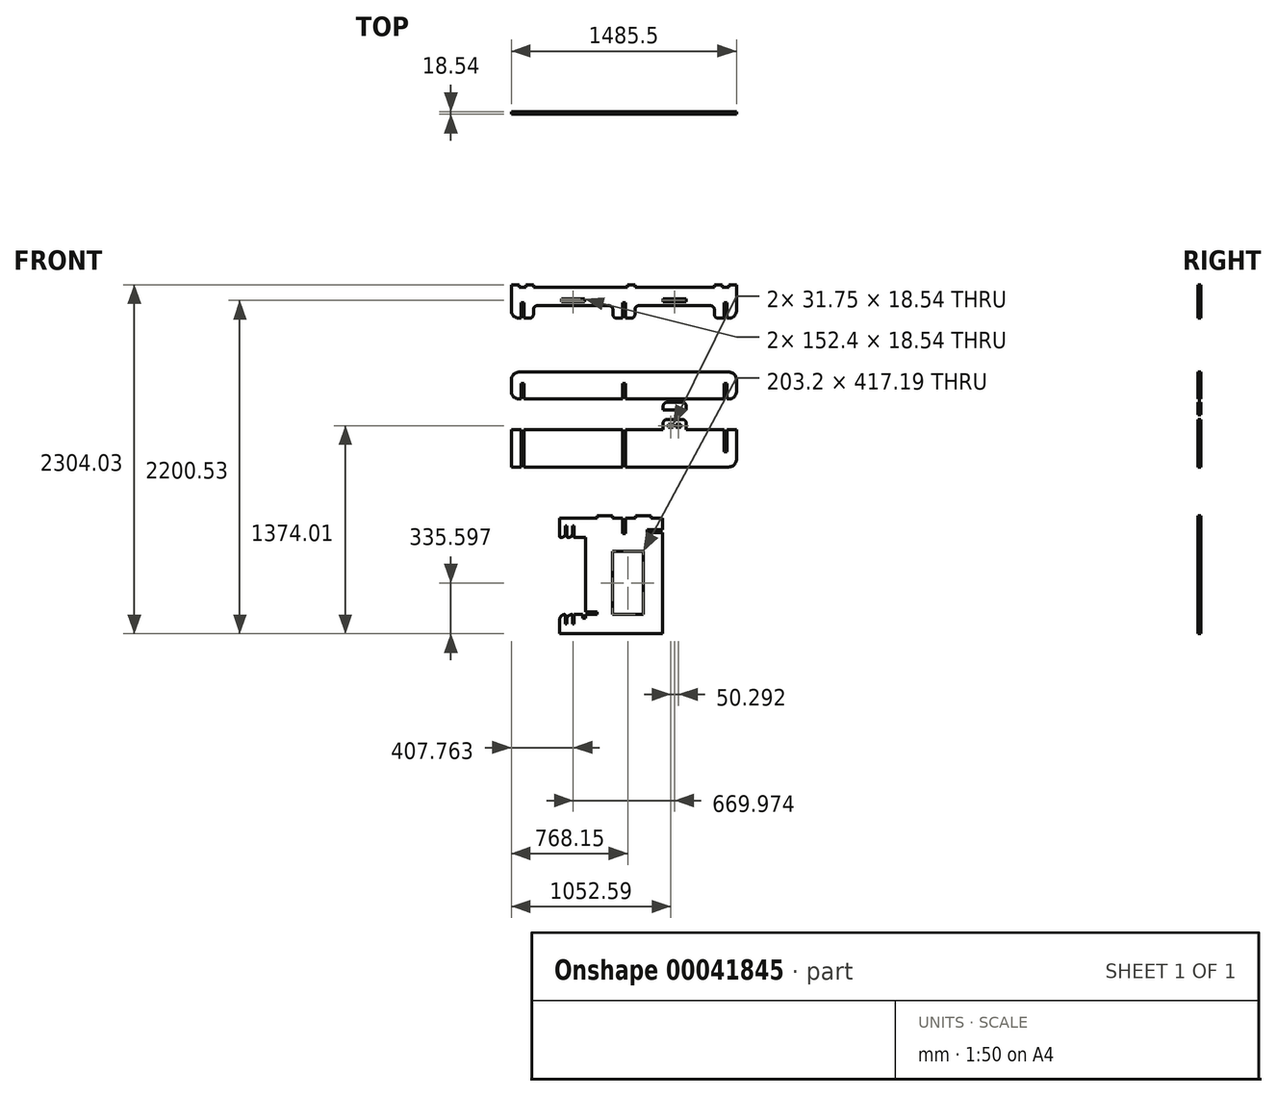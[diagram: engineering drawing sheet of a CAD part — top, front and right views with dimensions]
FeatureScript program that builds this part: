
annotation { "Feature Type Name" : "Feature", "Feature Type Description" : "" }
export const myFeature = defineFeature(function(context is Context, id is Id, definition is map)
    precondition{}
    {
        {
            var Q0;
            Q0=qCreatedBy(makeId("Front.planeOp"),FACE);
            var sketch = newSketch(context, id + "F0", { "sketchPlane" : qUnion([Q0])});
            skLineSegment(sketch, "E0.bottom", {"start": v(-254, 381) * mm, "end": v(-177.8, 381) * mm});
            skLineSegment(sketch, "E0.top", {"start": v(-254, -381) * mm, "end": v(254, -381) * mm});
            skLineSegment(sketch, "E0.left", {"start": v(-254, 254) * mm, "end": v(-254, -235.46) * mm});
            skLineSegment(sketch, "E0.right", {"start": v(254, 381) * mm, "end": v(254, -381) * mm});
            skLineSegment(sketch, "E1.bottom", {"start": v(-254, 381) * mm, "end": v(-423.33, 381) * mm});
            skLineSegment(sketch, "E1.top", {"start": v(-254, 254) * mm, "end": v(-323, 254) * mm});
            skLineSegment(sketch, "E1.right", {"start": v(-423.33, 381) * mm, "end": v(-423.33, 260.35) * mm});
            skLineSegment(sketch, "E2", {"start": v(-254, 0) * mm, "end": v(254, 0) * mm, "construction": true});
            skLineSegment(sketch, "E3", {"start": v(-423.33, 317.5) * mm, "end": v(-385.23, 317.5) * mm, "construction": true});
            skLineSegment(sketch, "E4.top", {"start": v(-385.23, 317.5) * mm, "end": v(-376.34, 317.5) * mm});
            skLineSegment(sketch, "E4.left", {"start": v(-385.23, 254) * mm, "end": v(-385.23, 317.5) * mm});
            skLineSegment(sketch, "E4.right", {"start": v(-376.34, 260.35) * mm, "end": v(-376.34, 317.5) * mm});
            skLineSegment(sketch, "E5", {"start": v(-376.34, 317.5) * mm, "end": v(-338.24, 317.5) * mm, "construction": true});
            skLineSegment(sketch, "E6.top", {"start": v(-338.24, 317.5) * mm, "end": v(-329.35, 317.5) * mm});
            skLineSegment(sketch, "E6.left", {"start": v(-338.24, 254) * mm, "end": v(-338.24, 317.5) * mm});
            skLineSegment(sketch, "E6.right", {"start": v(-329.35, 260.35) * mm, "end": v(-329.35, 317.5) * mm});
            skLineSegment(sketch, "E7.trimOffspring", {"start": v(-385.23, 254) * mm, "end": v(-416.98, 254) * mm});
            skLineSegment(sketch, "E8.trimOffspring", {"start": v(-338.24, 254) * mm, "end": v(-370, 254) * mm});
            skLineSegment(sketch, "E9.MirrorCS", {"start": v(-391.58, -254) * mm, "end": v(-423.33, -254) * mm});
            skLineSegment(sketch, "E10.MirrorCS", {"start": v(-376.34, -317.5) * mm, "end": v(-338.24, -317.5) * mm, "construction": true});
            skLineSegment(sketch, "E11.MirrorCS", {"start": v(-423.33, -317.5) * mm, "end": v(-385.23, -317.5) * mm, "construction": true});
            skLineSegment(sketch, "E12.MirrorCS", {"start": v(-338.24, -260.35) * mm, "end": v(-338.24, -317.5) * mm});
            skLineSegment(sketch, "E13.MirrorCS", {"start": v(-344.6, -254) * mm, "end": v(-376.34, -254) * mm});
            skLineSegment(sketch, "E14.MirrorCS", {"start": v(-423.33, -381) * mm, "end": v(-423.33, -254) * mm});
            skLineSegment(sketch, "E15.MirrorCS", {"start": v(-376.34, -254) * mm, "end": v(-376.34, -317.5) * mm});
            skLineSegment(sketch, "E16.MirrorCS", {"start": v(-385.23, -260.35) * mm, "end": v(-385.23, -317.5) * mm});
            skLineSegment(sketch, "E17.MirrorCS", {"start": v(-254, -381) * mm, "end": v(-423.33, -381) * mm});
            skLineSegment(sketch, "E18.MirrorCS", {"start": v(-385.23, -317.5) * mm, "end": v(-376.34, -317.5) * mm});
            skLineSegment(sketch, "E19.MirrorCS", {"start": v(-338.24, -317.5) * mm, "end": v(-329.35, -317.5) * mm});
            skLineSegment(sketch, "E20.MirrorCS", {"start": v(-329.35, -254) * mm, "end": v(-329.35, -317.5) * mm});
            skLineSegment(sketch, "E21.top", {"start": v(-177.8, 399.14) * mm, "end": v(-76.2, 399.14) * mm});
            skLineSegment(sketch, "E21.left", {"start": v(-177.8, 381) * mm, "end": v(-177.8, 399.14) * mm});
            skLineSegment(sketch, "E21.right", {"start": v(-76.2, 381) * mm, "end": v(-76.2, 399.14) * mm});
            skLineSegment(sketch, "E22", {"start": v(0, 381) * mm, "end": v(0, -381) * mm, "construction": true});
            skLineSegment(sketch, "E23.MirrorCS", {"start": v(177.8, 381) * mm, "end": v(177.8, 399.14) * mm});
            skLineSegment(sketch, "E24.MirrorCS", {"start": v(76.2, 381) * mm, "end": v(76.2, 399.14) * mm});
            skLineSegment(sketch, "E25.MirrorCS", {"start": v(177.8, 399.14) * mm, "end": v(76.2, 399.14) * mm});
            skLineSegment(sketch, "E26.left", {"start": v(-9.07, 381) * mm, "end": v(-9.07, 279.4) * mm});
            skPoint(sketch, "E27", {"position": v(0, 279.4) * mm});
            skLineSegment(sketch, "E26.right", {"start": v(9.07, 381) * mm, "end": v(9.07, 279.4) * mm});
            skPoint(sketch, "E28", {"position": v(0, 381) * mm});
            skLineSegment(sketch, "E26.bottom", {"start": v(-9.07, 381) * mm, "end": v(9.07, 381) * mm});
            skLineSegment(sketch, "E26.top", {"start": v(-9.07, 279.4) * mm, "end": v(9.07, 279.4) * mm});
            skLineSegment(sketch, "E29", {"start": v(25.4, 381) * mm, "end": v(25.4, 163.2) * mm, "construction": true});
            skLineSegment(sketch, "E30", {"start": v(254, -45.4) * mm, "end": v(127, -45.4) * mm, "construction": true});
            skLineSegment(sketch, "E31", {"start": v(0, -381) * mm, "end": v(0, -254) * mm, "construction": true});
            skLineSegment(sketch, "E32.bottom", {"start": v(-76.2, 163.2) * mm, "end": v(127, 163.2) * mm});
            skLineSegment(sketch, "E32.top", {"start": v(-76.2, -254) * mm, "end": v(127, -254) * mm});
            skLineSegment(sketch, "E32.left", {"start": v(-76.2, 163.2) * mm, "end": v(-76.2, -254) * mm});
            skLineSegment(sketch, "E32.right", {"start": v(127, 163.2) * mm, "end": v(127, -254) * mm});
            skLineSegment(sketch, "E33.right", {"start": v(-177.8, -254) * mm, "end": v(-177.8, -235.46) * mm});
            skLineSegment(sketch, "E34", {"start": v(-177.8, -235.46) * mm, "end": v(-254, -235.46) * mm});
            skPoint(sketch, "E35", {"position": v(0, 0) * mm});
            skLineSegment(sketch, "E36", {"start": v(-329.35, -254) * mm, "end": v(-177.8, -254) * mm});
            skLineSegment(sketch, "E37.trimOffspring", {"start": v(-76.2, 381) * mm, "end": v(76.2, 381) * mm});
            skLineSegment(sketch, "E38.trimOffspring", {"start": v(177.8, 381) * mm, "end": v(254, 381) * mm});
            skLineSegment(sketch, "E39.bottom", {"start": v(-177.8, -235.46) * mm, "end": v(-423.33, -235.46) * mm});
            skLineSegment(sketch, "E39.top", {"start": v(-177.8, -254) * mm, "end": v(-423.33, -254) * mm});
            skLineSegment(sketch, "E39.left", {"start": v(-177.8, -235.46) * mm, "end": v(-177.8, -254) * mm});
            skLineSegment(sketch, "E39.right", {"start": v(-423.33, -235.46) * mm, "end": v(-423.33, -254) * mm});
            skArc(sketch, "E40", {"start": v(-889.07, 2915.45) * mm, "mid": v(-449.45, 3014.68) * mm, "end": v(0, 3048) * mm});
            skArc(sketch, "E41.0", {"start": v(-656.32, 2189.76) * mm, "mid": v(-331.67, 2261.81) * mm, "end": v(0, 2286) * mm, "construction": true});
            skLineSegment(sketch, "E42", {"start": v(0, 3048) * mm, "end": v(0, 2718.2) * mm, "construction": true});
            skLineSegment(sketch, "E43", {"start": v(-719.24, 2222.78) * mm, "end": v(-739.7, 2286) * mm, "construction": true});
            skLineSegment(sketch, "E44", {"start": v(-703.77, 2174.97) * mm, "end": v(0, 0) * mm, "construction": true});
            skArc(sketch, "E45.MirrorCS", {"start": v(889.07, 2915.45) * mm, "mid": v(449.45, 3014.68) * mm, "end": v(0, 3048) * mm});
            skLineSegment(sketch, "E46.MirrorCS", {"start": v(719.24, 2222.78) * mm, "end": v(739.7, 2286) * mm, "construction": true});
            skArc(sketch, "E47.MirrorCS", {"start": v(656.32, 2189.76) * mm, "mid": v(331.67, 2261.81) * mm, "end": v(0, 2286) * mm, "construction": true});
            skLineSegment(sketch, "E48.MirrorCS", {"start": v(-9.27, 2362.2) * mm, "end": v(9.27, 2362.2) * mm});
            skLineSegment(sketch, "E49.MirrorCS", {"start": v(-9.27, 2362.2) * mm, "end": v(-9.27, 2463.8) * mm});
            skLineSegment(sketch, "E50.MirrorCS", {"start": v(-9.27, 2463.8) * mm, "end": v(9.27, 2463.8) * mm});
            skLineSegment(sketch, "E51.MirrorCS", {"start": v(9.27, 2362.2) * mm, "end": v(9.27, 2463.8) * mm});
            skLineSegment(sketch, "E52.left", {"start": v(-72.77, 2530.93) * mm, "end": v(-72.77, 2549.47) * mm});
            skLineSegment(sketch, "E52.bottom", {"start": v(-72.77, 2530.93) * mm, "end": v(-21.97, 2530.93) * mm});
            skLineSegment(sketch, "E52.top", {"start": v(-72.77, 2549.47) * mm, "end": v(-21.97, 2549.47) * mm});
            skLineSegment(sketch, "E52.right", {"start": v(-21.97, 2530.93) * mm, "end": v(-21.97, 2549.47) * mm});
            skPoint(sketch, "E53", {"position": v(-21.97, 2540.2) * mm});
            skLineSegment(sketch, "E54", {"start": v(0, 2286) * mm, "end": v(0, 2362.2) * mm});
            skPoint(sketch, "E55", {"position": v(0, 2362.2) * mm});
            skLineSegment(sketch, "E56", {"start": v(-9.27, 2463.8) * mm, "end": v(-9.27, 2530.93) * mm, "construction": true});
            skLineSegment(sketch, "E57", {"start": v(-9.27, 2530.93) * mm, "end": v(9.27, 2530.93) * mm, "construction": true});
            skPoint(sketch, "E58", {"position": v(0, 2530.93) * mm});
            skLineSegment(sketch, "E59.MirrorCS", {"start": v(21.97, 2530.93) * mm, "end": v(21.97, 2549.47) * mm});
            skPoint(sketch, "E60.MirrorP", {"position": v(21.97, 2540.2) * mm});
            skLineSegment(sketch, "E61.MirrorCS", {"start": v(72.77, 2530.93) * mm, "end": v(21.97, 2530.93) * mm});
            skLineSegment(sketch, "E62.MirrorCS", {"start": v(72.77, 2549.47) * mm, "end": v(21.97, 2549.47) * mm});
            skLineSegment(sketch, "E63.MirrorCS", {"start": v(72.77, 2530.93) * mm, "end": v(72.77, 2549.47) * mm});
            skLineSegment(sketch, "E64", {"start": v(-21.97, 2540.2) * mm, "end": v(21.97, 2540.2) * mm, "construction": true});
            skLineSegment(sketch, "E65.MirrorCS", {"start": v(-9.27, 2616.6) * mm, "end": v(9.27, 2616.6) * mm});
            skLineSegment(sketch, "E66.MirrorCS", {"start": v(9.27, 2718.2) * mm, "end": v(9.27, 2616.6) * mm});
            skLineSegment(sketch, "E67.MirrorCS", {"start": v(-9.27, 2718.2) * mm, "end": v(-9.27, 2616.6) * mm});
            skLineSegment(sketch, "E68.MirrorCS", {"start": v(-9.27, 2718.2) * mm, "end": v(9.27, 2718.2) * mm});
            skLineSegment(sketch, "E69", {"start": v(-764.35, 2362.2) * mm, "end": v(764.35, 2362.2) * mm, "construction": true});
            skLineSegment(sketch, "E70", {"start": v(-818.95, 2530.93) * mm, "end": v(-742.75, 2530.93) * mm, "construction": true});
            skLineSegment(sketch, "E71.trimOffspring", {"start": v(0, 2616.6) * mm, "end": v(0, 2463.8) * mm, "construction": true});
            skLineSegment(sketch, "E72.trimOffspring", {"start": v(0, 2362.2) * mm, "end": v(0, 2286) * mm, "construction": true});
            skLineSegment(sketch, "E73.MirrorCS", {"start": v(-679.25, 2362.2) * mm, "end": v(-660.7, 2362.2) * mm});
            skLineSegment(sketch, "E74.MirrorCS", {"start": v(-679.25, 2362.2) * mm, "end": v(-679.25, 2463.8) * mm});
            skLineSegment(sketch, "E75.MirrorCS", {"start": v(-679.25, 2463.8) * mm, "end": v(-660.7, 2463.8) * mm});
            skLineSegment(sketch, "E76.MirrorCS", {"start": v(-660.7, 2362.2) * mm, "end": v(-660.7, 2463.8) * mm});
            skLineSegment(sketch, "E77.left", {"start": v(-742.75, 2530.93) * mm, "end": v(-742.75, 2549.47) * mm});
            skLineSegment(sketch, "E77.bottom", {"start": v(-742.75, 2530.93) * mm, "end": v(-691.95, 2530.93) * mm});
            skLineSegment(sketch, "E77.top", {"start": v(-742.75, 2549.47) * mm, "end": v(-691.95, 2549.47) * mm});
            skLineSegment(sketch, "E77.right", {"start": v(-691.95, 2530.93) * mm, "end": v(-691.95, 2549.47) * mm});
            skPoint(sketch, "E78", {"position": v(-691.95, 2540.2) * mm});
            skPoint(sketch, "E79", {"position": v(-669.97, 2362.2) * mm});
            skLineSegment(sketch, "E80", {"start": v(-679.25, 2463.8) * mm, "end": v(-679.25, 2530.93) * mm, "construction": true});
            skLineSegment(sketch, "E81", {"start": v(-679.25, 2530.93) * mm, "end": v(-660.7, 2530.93) * mm, "construction": true});
            skPoint(sketch, "E82", {"position": v(-669.97, 2530.93) * mm});
            skLineSegment(sketch, "E83.MirrorCS", {"start": v(-648, 2530.93) * mm, "end": v(-648, 2549.47) * mm});
            skPoint(sketch, "E84.MirrorP", {"position": v(-648, 2540.2) * mm});
            skLineSegment(sketch, "E85.MirrorCS", {"start": v(-597.2, 2530.93) * mm, "end": v(-648, 2530.93) * mm});
            skLineSegment(sketch, "E86.MirrorCS", {"start": v(-597.2, 2549.47) * mm, "end": v(-648, 2549.47) * mm});
            skLineSegment(sketch, "E87.MirrorCS", {"start": v(-597.2, 2530.93) * mm, "end": v(-597.2, 2549.47) * mm});
            skLineSegment(sketch, "E88", {"start": v(-648, 2540.2) * mm, "end": v(-691.95, 2540.2) * mm, "construction": true});
            skLineSegment(sketch, "E89.MirrorCS", {"start": v(-679.25, 2616.6) * mm, "end": v(-660.7, 2616.6) * mm});
            skLineSegment(sketch, "E90.MirrorCS", {"start": v(-660.7, 2718.2) * mm, "end": v(-660.7, 2616.6) * mm});
            skLineSegment(sketch, "E91.MirrorCS", {"start": v(-679.25, 2718.2) * mm, "end": v(-679.25, 2616.6) * mm});
            skLineSegment(sketch, "E92.MirrorCS", {"start": v(-679.25, 2718.2) * mm, "end": v(-660.7, 2718.2) * mm});
            skLineSegment(sketch, "E93.trimOffspring", {"start": v(-669.97, 2463.8) * mm, "end": v(-669.97, 2616.6) * mm, "construction": true});
            skLineSegment(sketch, "E94.MirrorCS", {"start": v(679.25, 2718.2) * mm, "end": v(660.7, 2718.2) * mm});
            skLineSegment(sketch, "E95.MirrorCS", {"start": v(679.25, 2718.2) * mm, "end": v(679.25, 2616.6) * mm});
            skLineSegment(sketch, "E96.MirrorCS", {"start": v(660.7, 2718.2) * mm, "end": v(660.7, 2616.6) * mm});
            skLineSegment(sketch, "E97.MirrorCS", {"start": v(679.25, 2616.6) * mm, "end": v(660.7, 2616.6) * mm});
            skLineSegment(sketch, "E98.MirrorCS", {"start": v(742.75, 2549.47) * mm, "end": v(691.95, 2549.47) * mm});
            skLineSegment(sketch, "E99.MirrorCS", {"start": v(742.75, 2530.93) * mm, "end": v(742.75, 2549.47) * mm});
            skLineSegment(sketch, "E100.MirrorCS", {"start": v(691.95, 2530.93) * mm, "end": v(691.95, 2549.47) * mm});
            skLineSegment(sketch, "E101.MirrorCS", {"start": v(742.75, 2530.93) * mm, "end": v(691.95, 2530.93) * mm});
            skLineSegment(sketch, "E102.MirrorCS", {"start": v(648, 2530.93) * mm, "end": v(648, 2549.47) * mm});
            skLineSegment(sketch, "E103.MirrorCS", {"start": v(597.2, 2549.47) * mm, "end": v(648, 2549.47) * mm});
            skLineSegment(sketch, "E104.MirrorCS", {"start": v(597.2, 2530.93) * mm, "end": v(597.2, 2549.47) * mm});
            skLineSegment(sketch, "E105.MirrorCS", {"start": v(597.2, 2530.93) * mm, "end": v(648, 2530.93) * mm});
            skLineSegment(sketch, "E106.MirrorCS", {"start": v(679.25, 2362.2) * mm, "end": v(660.7, 2362.2) * mm});
            skLineSegment(sketch, "E107.MirrorCS", {"start": v(679.25, 2362.2) * mm, "end": v(679.25, 2463.8) * mm});
            skLineSegment(sketch, "E108.MirrorCS", {"start": v(660.7, 2362.2) * mm, "end": v(660.7, 2463.8) * mm});
            skLineSegment(sketch, "E109.MirrorCS", {"start": v(679.25, 2463.8) * mm, "end": v(660.7, 2463.8) * mm});
            skLineSegment(sketch, "E110.bottom", {"start": v(-742.75, 1905) * mm, "end": v(-691.95, 1905) * mm});
            skLineSegment(sketch, "E110.top", {"start": v(-742.75, 1923.03) * mm, "end": v(-691.95, 1923.03) * mm});
            skLineSegment(sketch, "E110.left", {"start": v(-742.75, 1905) * mm, "end": v(-742.75, 1923.03) * mm});
            skLineSegment(sketch, "E110.right", {"start": v(-691.95, 1905) * mm, "end": v(-691.95, 1923.03) * mm});
            skLineSegment(sketch, "E111.bottom", {"start": v(-742.75, 1905) * mm, "end": v(742.75, 1905) * mm});
            skLineSegment(sketch, "E111.top", {"start": v(-691.95, 1701.8) * mm, "end": v(-622.6, 1701.8) * mm});
            skLineSegment(sketch, "E111.left", {"start": v(-742.75, 1905) * mm, "end": v(-742.75, 1752.6) * mm});
            skLineSegment(sketch, "E111.right", {"start": v(742.75, 1905) * mm, "end": v(742.75, 1752.6) * mm});
            skLineSegment(sketch, "E112", {"start": v(-742.75, 1803.4) * mm, "end": v(-679.25, 1803.4) * mm, "construction": true});
            skLineSegment(sketch, "E113.bottom", {"start": v(-679.25, 1701.8) * mm, "end": v(-660.7, 1701.8) * mm});
            skLineSegment(sketch, "E113.top", {"start": v(-679.25, 1803.4) * mm, "end": v(-660.7, 1803.4) * mm});
            skLineSegment(sketch, "E113.left", {"start": v(-679.25, 1701.8) * mm, "end": v(-679.25, 1803.4) * mm});
            skLineSegment(sketch, "E113.right", {"start": v(-660.7, 1701.8) * mm, "end": v(-660.7, 1803.4) * mm});
            skLineSegment(sketch, "E114", {"start": v(-669.97, 1803.4) * mm, "end": v(-669.97, 1905) * mm, "construction": true});
            skLineSegment(sketch, "E115.MirrorCS", {"start": v(-648, 1905) * mm, "end": v(-648, 1923.03) * mm});
            skLineSegment(sketch, "E116.MirrorCS", {"start": v(-597.2, 1923.03) * mm, "end": v(-648, 1923.03) * mm});
            skLineSegment(sketch, "E117.MirrorCS", {"start": v(-597.2, 1905) * mm, "end": v(-597.2, 1923.03) * mm});
            skLineSegment(sketch, "E118", {"start": v(0, 1905) * mm, "end": v(0, 1701.8) * mm, "construction": true});
            skLineSegment(sketch, "E119.MirrorCS", {"start": v(742.75, 1923.03) * mm, "end": v(691.95, 1923.03) * mm});
            skLineSegment(sketch, "E120.MirrorCS", {"start": v(742.75, 1905) * mm, "end": v(742.75, 1923.03) * mm});
            skLineSegment(sketch, "E121.MirrorCS", {"start": v(742.75, 1905) * mm, "end": v(691.95, 1905) * mm});
            skLineSegment(sketch, "E122.MirrorCS", {"start": v(691.95, 1905) * mm, "end": v(691.95, 1923.03) * mm});
            skLineSegment(sketch, "E123.MirrorCS", {"start": v(597.2, 1905) * mm, "end": v(597.2, 1923.03) * mm});
            skLineSegment(sketch, "E124.MirrorCS", {"start": v(648, 1905) * mm, "end": v(648, 1923.03) * mm});
            skLineSegment(sketch, "E125.MirrorCS", {"start": v(597.2, 1923.03) * mm, "end": v(648, 1923.03) * mm});
            skLineSegment(sketch, "E126.MirrorCS", {"start": v(679.25, 1803.4) * mm, "end": v(660.7, 1803.4) * mm});
            skLineSegment(sketch, "E127.MirrorCS", {"start": v(660.7, 1701.8) * mm, "end": v(660.7, 1803.4) * mm});
            skLineSegment(sketch, "E128.MirrorCS", {"start": v(679.25, 1701.8) * mm, "end": v(660.7, 1701.8) * mm});
            skLineSegment(sketch, "E129.MirrorCS", {"start": v(679.25, 1701.8) * mm, "end": v(679.25, 1803.4) * mm});
            skLineSegment(sketch, "E130.bottom", {"start": v(-72.77, 1905) * mm, "end": v(-21.97, 1905) * mm});
            skLineSegment(sketch, "E130.top", {"start": v(-72.77, 1923.03) * mm, "end": v(-21.97, 1923.03) * mm});
            skLineSegment(sketch, "E130.left", {"start": v(-72.77, 1905) * mm, "end": v(-72.77, 1923.03) * mm});
            skLineSegment(sketch, "E130.right", {"start": v(-21.97, 1905) * mm, "end": v(-21.97, 1923.03) * mm});
            skLineSegment(sketch, "E131.bottom", {"start": v(-9.27, 1701.8) * mm, "end": v(9.27, 1701.8) * mm});
            skLineSegment(sketch, "E131.top", {"start": v(-9.27, 1803.4) * mm, "end": v(9.27, 1803.4) * mm});
            skLineSegment(sketch, "E131.left", {"start": v(-9.27, 1701.8) * mm, "end": v(-9.27, 1803.4) * mm});
            skLineSegment(sketch, "E131.right", {"start": v(9.27, 1701.8) * mm, "end": v(9.27, 1803.4) * mm});
            skPoint(sketch, "E132", {"position": v(0, 1701.8) * mm});
            skLineSegment(sketch, "E133.MirrorCS", {"start": v(21.97, 1905) * mm, "end": v(21.97, 1923.03) * mm});
            skLineSegment(sketch, "E134.MirrorCS", {"start": v(72.77, 1905) * mm, "end": v(72.77, 1923.03) * mm});
            skLineSegment(sketch, "E135.MirrorCS", {"start": v(72.77, 1923.03) * mm, "end": v(21.97, 1923.03) * mm});
            skLineSegment(sketch, "E136.MirrorCS", {"start": v(72.77, 1905) * mm, "end": v(21.97, 1905) * mm});
            skPoint(sketch, "E137.visualSharp", {"position": v(-742.75, 1701.8) * mm});
            skArc(sketch, "E137.filletArc", {"start": v(-742.75, 1752.6) * mm, "mid": v(-727.87, 1716.68) * mm, "end": v(-691.95, 1701.8) * mm});
            skPoint(sketch, "E138.visualSharp", {"position": v(742.75, 1701.8) * mm});
            skArc(sketch, "E138.filletArc", {"start": v(691.95, 1701.8) * mm, "mid": v(727.87, 1716.68) * mm, "end": v(742.75, 1752.6) * mm});
            skPoint(sketch, "E139.visualSharp", {"position": v(-703.77, 2174.97) * mm});
            skArc(sketch, "E139.filletArc", {"start": v(-719.24, 2222.78) * mm, "mid": v(-694.51, 2193.44) * mm, "end": v(-656.32, 2189.76) * mm, "construction": true});
            skPoint(sketch, "E140.visualSharp", {"position": v(703.77, 2174.97) * mm});
            skArc(sketch, "E140.filletArc", {"start": v(656.32, 2189.76) * mm, "mid": v(694.51, 2193.44) * mm, "end": v(719.24, 2222.78) * mm, "construction": true});
            skPoint(sketch, "E141.visualSharp", {"position": v(938.35, 2899.96) * mm});
            skArc(sketch, "E141.filletArc", {"start": v(922.58, 2851.22) * mm, "mid": v(919.29, 2890.36) * mm, "end": v(889.07, 2915.45) * mm});
            skPoint(sketch, "E142.visualSharp", {"position": v(-938.35, 2899.96) * mm});
            skArc(sketch, "E142.filletArc", {"start": v(-889.07, 2915.45) * mm, "mid": v(-919.29, 2890.36) * mm, "end": v(-922.58, 2851.22) * mm});
            skLineSegment(sketch, "E143.bottom", {"start": v(-691.95, 1346.2) * mm, "end": v(691.95, 1346.2) * mm});
            skLineSegment(sketch, "E143.top", {"start": v(-691.95, 1168.4) * mm, "end": v(691.95, 1168.4) * mm});
            skLineSegment(sketch, "E143.left", {"start": v(-742.75, 1295.4) * mm, "end": v(-742.75, 1219.2) * mm});
            skLineSegment(sketch, "E143.right", {"start": v(742.75, 1295.4) * mm, "end": v(742.75, 1219.2) * mm});
            skPoint(sketch, "E144", {"position": v(0, 1168.4) * mm});
            skLineSegment(sketch, "E145.bottom", {"start": v(-679.25, 1168.4) * mm, "end": v(-660.7, 1168.4) * mm});
            skLineSegment(sketch, "E145.top", {"start": v(-679.25, 1270) * mm, "end": v(-660.7, 1270) * mm});
            skLineSegment(sketch, "E145.left", {"start": v(-679.25, 1168.4) * mm, "end": v(-679.25, 1270) * mm});
            skLineSegment(sketch, "E145.right", {"start": v(-660.7, 1168.4) * mm, "end": v(-660.7, 1270) * mm});
            skLineSegment(sketch, "E146", {"start": v(0, 1346.2) * mm, "end": v(0, 1168.4) * mm, "construction": true});
            skLineSegment(sketch, "E147.bottom", {"start": v(-9.27, 1168.4) * mm, "end": v(9.27, 1168.4) * mm});
            skLineSegment(sketch, "E147.top", {"start": v(-9.27, 1270) * mm, "end": v(9.27, 1270) * mm});
            skLineSegment(sketch, "E147.left", {"start": v(-9.27, 1168.4) * mm, "end": v(-9.27, 1270) * mm});
            skLineSegment(sketch, "E147.right", {"start": v(9.27, 1168.4) * mm, "end": v(9.27, 1270) * mm});
            skLineSegment(sketch, "E148.MirrorCS", {"start": v(660.7, 1168.4) * mm, "end": v(660.7, 1270) * mm});
            skLineSegment(sketch, "E149.MirrorCS", {"start": v(679.25, 1168.4) * mm, "end": v(679.25, 1270) * mm});
            skLineSegment(sketch, "E150.MirrorCS", {"start": v(679.25, 1168.4) * mm, "end": v(660.7, 1168.4) * mm});
            skLineSegment(sketch, "E151.MirrorCS", {"start": v(679.25, 1270) * mm, "end": v(660.7, 1270) * mm});
            skPoint(sketch, "E152.visualSharp", {"position": v(-742.75, 1346.2) * mm});
            skArc(sketch, "E152.filletArc", {"start": v(-691.95, 1346.2) * mm, "mid": v(-727.87, 1331.32) * mm, "end": v(-742.75, 1295.4) * mm});
            skPoint(sketch, "E153.visualSharp", {"position": v(-742.75, 1168.4) * mm});
            skArc(sketch, "E153.filletArc", {"start": v(-742.75, 1219.2) * mm, "mid": v(-727.87, 1183.28) * mm, "end": v(-691.95, 1168.4) * mm});
            skPoint(sketch, "E154.visualSharp", {"position": v(742.75, 1346.2) * mm});
            skArc(sketch, "E154.filletArc", {"start": v(742.75, 1295.4) * mm, "mid": v(727.87, 1331.32) * mm, "end": v(691.95, 1346.2) * mm});
            skPoint(sketch, "E155.visualSharp", {"position": v(742.75, 1168.4) * mm});
            skArc(sketch, "E155.filletArc", {"start": v(691.95, 1168.4) * mm, "mid": v(727.87, 1183.28) * mm, "end": v(742.75, 1219.2) * mm});
            skLineSegment(sketch, "E156.bottom", {"start": v(254, 286.26) * mm, "end": v(152.4, 286.26) * mm});
            skLineSegment(sketch, "E156.top", {"start": v(254, 304.8) * mm, "end": v(152.4, 304.8) * mm});
            skLineSegment(sketch, "E156.left", {"start": v(254, 286.26) * mm, "end": v(254, 304.8) * mm});
            skLineSegment(sketch, "E156.right", {"start": v(152.4, 286.26) * mm, "end": v(152.4, 304.8) * mm});
            skLineSegment(sketch, "E157", {"start": v(-334.99, 1905) * mm, "end": v(-334.99, 1810.26) * mm, "construction": true});
            skPoint(sketch, "E157.startSnap0", {"position": v(-334.99, 1784.86) * mm});
            skLineSegment(sketch, "E158.bottom", {"start": v(-411.19, 1810.26) * mm, "end": v(-258.79, 1810.26) * mm});
            skLineSegment(sketch, "E158.top", {"start": v(-411.19, 1828.8) * mm, "end": v(-258.79, 1828.8) * mm});
            skLineSegment(sketch, "E158.left", {"start": v(-411.19, 1810.26) * mm, "end": v(-411.19, 1828.8) * mm});
            skLineSegment(sketch, "E158.right", {"start": v(-258.79, 1810.26) * mm, "end": v(-258.79, 1828.8) * mm});
            skLineSegment(sketch, "E159.MirrorCS", {"start": v(258.79, 1810.26) * mm, "end": v(258.79, 1828.8) * mm});
            skLineSegment(sketch, "E160.MirrorCS", {"start": v(411.19, 1810.26) * mm, "end": v(411.19, 1828.8) * mm});
            skLineSegment(sketch, "E161.MirrorCS", {"start": v(411.19, 1810.26) * mm, "end": v(258.79, 1810.26) * mm});
            skLineSegment(sketch, "E162.MirrorCS", {"start": v(411.19, 1828.8) * mm, "end": v(258.79, 1828.8) * mm});
            skLineSegment(sketch, "E163.bottom", {"start": v(-742.75, 965.2) * mm, "end": v(742.75, 965.2) * mm});
            skLineSegment(sketch, "E163.top", {"start": v(-742.75, 720.27) * mm, "end": v(691.95, 720.27) * mm});
            skLineSegment(sketch, "E163.left", {"start": v(-742.75, 965.2) * mm, "end": v(-742.75, 720.27) * mm});
            skLineSegment(sketch, "E163.right", {"start": v(742.75, 965.2) * mm, "end": v(742.75, 771.07) * mm});
            skPoint(sketch, "E164", {"position": v(0, 720.27) * mm});
            skLineSegment(sketch, "E165.bottom", {"start": v(-679.25, 720.27) * mm, "end": v(-660.7, 720.27) * mm});
            skLineSegment(sketch, "E165.top", {"start": v(-679.25, 821.87) * mm, "end": v(-660.7, 821.87) * mm});
            skLineSegment(sketch, "E165.left", {"start": v(-679.25, 720.27) * mm, "end": v(-679.25, 821.87) * mm});
            skLineSegment(sketch, "E165.right", {"start": v(-660.7, 720.27) * mm, "end": v(-660.7, 821.87) * mm});
            skLineSegment(sketch, "E166", {"start": v(0, 965.2) * mm, "end": v(0, 720.27) * mm, "construction": true});
            skLineSegment(sketch, "E167.bottom", {"start": v(-9.27, 720.27) * mm, "end": v(9.27, 720.27) * mm});
            skLineSegment(sketch, "E167.top", {"start": v(-9.27, 821.87) * mm, "end": v(9.27, 821.87) * mm});
            skLineSegment(sketch, "E167.left", {"start": v(-9.27, 720.27) * mm, "end": v(-9.27, 821.87) * mm});
            skLineSegment(sketch, "E167.right", {"start": v(9.27, 720.27) * mm, "end": v(9.27, 821.87) * mm});
            skLineSegment(sketch, "E168.MirrorCS", {"start": v(660.7, 720.27) * mm, "end": v(660.7, 821.87) * mm});
            skLineSegment(sketch, "E169.MirrorCS", {"start": v(679.25, 720.27) * mm, "end": v(679.25, 821.87) * mm});
            skLineSegment(sketch, "E170.MirrorCS", {"start": v(679.25, 720.27) * mm, "end": v(660.7, 720.27) * mm});
            skLineSegment(sketch, "E171.MirrorCS", {"start": v(679.25, 821.87) * mm, "end": v(660.7, 821.87) * mm});
            skPoint(sketch, "E172.visualSharp", {"position": v(-742.75, 965.2) * mm});
            skLineSegment(sketch, "E172.filletArc", {"start": v(-742.75, 965.2) * mm, "end": v(-742.75, 965.2) * mm});
            skPoint(sketch, "E173.visualSharp", {"position": v(-742.75, 720.27) * mm});
            skLineSegment(sketch, "E173.filletArc", {"start": v(-742.75, 720.27) * mm, "end": v(-742.75, 720.27) * mm});
            skPoint(sketch, "E174.visualSharp", {"position": v(742.75, 965.2) * mm});
            skLineSegment(sketch, "E174.filletArc", {"start": v(742.75, 965.2) * mm, "end": v(742.75, 965.2) * mm});
            skPoint(sketch, "E175.visualSharp", {"position": v(742.75, 720.27) * mm});
            skArc(sketch, "E175.filletArc", {"start": v(691.95, 720.27) * mm, "mid": v(727.87, 735.15) * mm, "end": v(742.75, 771.07) * mm});
            skLineSegment(sketch, "E176.bottom", {"start": v(-411.19, 965.2) * mm, "end": v(-258.79, 965.2) * mm});
            skLineSegment(sketch, "E176.top", {"start": v(-385.79, 1034.03) * mm, "end": v(-284.19, 1034.03) * mm});
            skLineSegment(sketch, "E176.left", {"start": v(-411.19, 965.2) * mm, "end": v(-411.19, 1008.63) * mm});
            skLineSegment(sketch, "E176.right", {"start": v(-258.79, 965.2) * mm, "end": v(-258.79, 1008.63) * mm});
            skLineSegment(sketch, "E177.top", {"start": v(-679.25, 965.2) * mm, "end": v(-660.7, 965.2) * mm});
            skLineSegment(sketch, "E177.left", {"start": v(-679.25, 821.87) * mm, "end": v(-679.25, 965.2) * mm});
            skLineSegment(sketch, "E177.right", {"start": v(-660.7, 821.87) * mm, "end": v(-660.7, 965.2) * mm});
            skLineSegment(sketch, "E178.top", {"start": v(-9.27, 965.2) * mm, "end": v(9.27, 965.2) * mm});
            skLineSegment(sketch, "E178.left", {"start": v(-9.27, 821.87) * mm, "end": v(-9.27, 965.2) * mm});
            skLineSegment(sketch, "E178.right", {"start": v(9.27, 821.87) * mm, "end": v(9.27, 965.2) * mm});
            skLineSegment(sketch, "E179.bottom", {"start": v(660.7, 821.87) * mm, "end": v(679.25, 821.87) * mm});
            skLineSegment(sketch, "E179.top", {"start": v(660.7, 965.2) * mm, "end": v(679.25, 965.2) * mm});
            skLineSegment(sketch, "E179.left", {"start": v(660.7, 821.87) * mm, "end": v(660.7, 965.2) * mm});
            skLineSegment(sketch, "E179.right", {"start": v(679.25, 821.87) * mm, "end": v(679.25, 965.2) * mm});
            skPoint(sketch, "E180.start.orphan", {"position": v(-334.99, 965.2) * mm});
            skLineSegment(sketch, "E181.bottom", {"start": v(-376, 1002.28) * mm, "end": v(-344.26, 1002.28) * mm});
            skLineSegment(sketch, "E181.top", {"start": v(-376, 983.74) * mm, "end": v(-344.26, 983.74) * mm});
            skLineSegment(sketch, "E181.left", {"start": v(-376, 1002.28) * mm, "end": v(-376, 983.74) * mm});
            skLineSegment(sketch, "E181.right", {"start": v(-344.26, 1002.28) * mm, "end": v(-344.26, 983.74) * mm});
            skLineSegment(sketch, "E182", {"start": v(-334.99, 965.2) * mm, "end": v(-334.99, 1034.03) * mm, "construction": true});
            skLineSegment(sketch, "E183.MirrorCS", {"start": v(-325.72, 1002.28) * mm, "end": v(-325.72, 983.74) * mm});
            skLineSegment(sketch, "E184.MirrorCS", {"start": v(-293.97, 1002.28) * mm, "end": v(-293.97, 983.74) * mm});
            skLineSegment(sketch, "E185.MirrorCS", {"start": v(-293.97, 983.74) * mm, "end": v(-325.72, 983.74) * mm});
            skLineSegment(sketch, "E186.MirrorCS", {"start": v(-293.97, 1002.28) * mm, "end": v(-325.72, 1002.28) * mm});
            skLineSegment(sketch, "E187.MirrorCS", {"start": v(344.26, 1002.28) * mm, "end": v(344.26, 983.74) * mm});
            skLineSegment(sketch, "E188.MirrorCS", {"start": v(376, 1002.28) * mm, "end": v(376, 983.74) * mm});
            skLineSegment(sketch, "E189.MirrorCS", {"start": v(293.97, 1002.28) * mm, "end": v(293.97, 983.74) * mm});
            skLineSegment(sketch, "E190.MirrorCS", {"start": v(325.72, 1002.28) * mm, "end": v(325.72, 983.74) * mm});
            skLineSegment(sketch, "E191.MirrorCS", {"start": v(376, 983.74) * mm, "end": v(344.26, 983.74) * mm});
            skLineSegment(sketch, "E192.MirrorCS", {"start": v(376, 1002.28) * mm, "end": v(344.26, 1002.28) * mm});
            skLineSegment(sketch, "E193.MirrorCS", {"start": v(293.97, 1002.28) * mm, "end": v(325.72, 1002.28) * mm});
            skLineSegment(sketch, "E194.MirrorCS", {"start": v(334.99, 965.2) * mm, "end": v(334.99, 1034.03) * mm, "construction": true});
            skLineSegment(sketch, "E195.MirrorCS", {"start": v(258.79, 965.2) * mm, "end": v(258.79, 1008.63) * mm});
            skLineSegment(sketch, "E196.MirrorCS", {"start": v(411.19, 965.2) * mm, "end": v(411.19, 1008.63) * mm});
            skLineSegment(sketch, "E197.MirrorCS", {"start": v(411.19, 965.2) * mm, "end": v(258.79, 965.2) * mm});
            skLineSegment(sketch, "E198.MirrorCS", {"start": v(385.79, 1034.03) * mm, "end": v(284.19, 1034.03) * mm});
            skPoint(sketch, "E199.MirrorP", {"position": v(334.99, 965.2) * mm});
            skLineSegment(sketch, "E200.MirrorCS", {"start": v(293.97, 983.74) * mm, "end": v(325.72, 983.74) * mm});
            skLineSegment(sketch, "E201.bottom", {"start": v(-254, -254) * mm, "end": v(-272.54, -254) * mm});
            skLineSegment(sketch, "E201.top", {"start": v(-254, -279.4) * mm, "end": v(-272.54, -279.4) * mm});
            skLineSegment(sketch, "E201.left", {"start": v(-254, -254) * mm, "end": v(-254, -279.4) * mm});
            skLineSegment(sketch, "E201.right", {"start": v(-272.54, -254) * mm, "end": v(-272.54, -279.4) * mm});
            skLineSegment(sketch, "E202.bottom", {"start": v(284.19, 1146.43) * mm, "end": v(385.79, 1146.43) * mm});
            skLineSegment(sketch, "E202.top", {"start": v(258.79, 1095.63) * mm, "end": v(411.19, 1095.63) * mm});
            skLineSegment(sketch, "E202.left", {"start": v(258.79, 1121.03) * mm, "end": v(258.79, 1095.63) * mm});
            skLineSegment(sketch, "E202.right", {"start": v(411.19, 1121.03) * mm, "end": v(411.19, 1095.63) * mm});
            skLineSegment(sketch, "E203.bottom", {"start": v(293.97, 1095.63) * mm, "end": v(325.72, 1095.63) * mm});
            skLineSegment(sketch, "E203.top", {"start": v(293.97, 1063.88) * mm, "end": v(325.72, 1063.88) * mm});
            skLineSegment(sketch, "E203.left", {"start": v(293.97, 1095.63) * mm, "end": v(293.97, 1063.88) * mm});
            skLineSegment(sketch, "E203.right", {"start": v(325.72, 1095.63) * mm, "end": v(325.72, 1063.88) * mm});
            skLineSegment(sketch, "E204.MirrorCS", {"start": v(344.26, 1095.63) * mm, "end": v(344.26, 1063.88) * mm});
            skLineSegment(sketch, "E205.MirrorCS", {"start": v(376, 1063.88) * mm, "end": v(344.26, 1063.88) * mm});
            skLineSegment(sketch, "E206.MirrorCS", {"start": v(376, 1095.63) * mm, "end": v(376, 1063.88) * mm});
            skLineSegment(sketch, "E207.MirrorCS", {"start": v(376, 1095.63) * mm, "end": v(344.26, 1095.63) * mm});
            skPoint(sketch, "E208.visualSharp", {"position": v(-411.19, 1034.03) * mm});
            skArc(sketch, "E208.filletArc", {"start": v(-385.79, 1034.03) * mm, "mid": v(-403.75, 1026.6) * mm, "end": v(-411.19, 1008.63) * mm});
            skPoint(sketch, "E209.visualSharp", {"position": v(-258.79, 1034.03) * mm});
            skArc(sketch, "E209.filletArc", {"start": v(-258.79, 1008.63) * mm, "mid": v(-266.23, 1026.6) * mm, "end": v(-284.19, 1034.03) * mm});
            skPoint(sketch, "E210.visualSharp", {"position": v(258.79, 1034.03) * mm});
            skArc(sketch, "E210.filletArc", {"start": v(284.19, 1034.03) * mm, "mid": v(266.23, 1026.6) * mm, "end": v(258.79, 1008.63) * mm});
            skPoint(sketch, "E211.visualSharp", {"position": v(411.19, 1034.03) * mm});
            skArc(sketch, "E211.filletArc", {"start": v(411.19, 1008.63) * mm, "mid": v(403.75, 1026.6) * mm, "end": v(385.79, 1034.03) * mm});
            skPoint(sketch, "E212.visualSharp", {"position": v(258.79, 1146.43) * mm});
            skArc(sketch, "E212.filletArc", {"start": v(284.19, 1146.43) * mm, "mid": v(266.23, 1139) * mm, "end": v(258.79, 1121.03) * mm});
            skPoint(sketch, "E213.visualSharp", {"position": v(411.19, 1146.43) * mm});
            skArc(sketch, "E213.filletArc", {"start": v(411.19, 1121.03) * mm, "mid": v(403.75, 1139) * mm, "end": v(385.79, 1146.43) * mm});
            skLineSegment(sketch, "E214", {"start": v(-597.2, 1727.2) * mm, "end": v(-597.2, 1759.46) * mm});
            skLineSegment(sketch, "E215", {"start": v(-571.8, 1784.86) * mm, "end": v(-98.17, 1784.86) * mm});
            skLineSegment(sketch, "E216", {"start": v(-72.77, 1759.46) * mm, "end": v(-72.77, 1727.2) * mm});
            skPoint(sketch, "E217.visualSharp", {"position": v(-597.2, 1784.86) * mm});
            skArc(sketch, "E217.filletArc", {"start": v(-571.8, 1784.86) * mm, "mid": v(-589.76, 1777.42) * mm, "end": v(-597.2, 1759.46) * mm});
            skLineSegment(sketch, "E218", {"start": v(-597.2, 1701.8) * mm, "end": v(-72.77, 1701.8) * mm, "construction": true});
            skLineSegment(sketch, "E219", {"start": v(-47.37, 1701.8) * mm, "end": v(72.1, 1701.8) * mm});
            skPoint(sketch, "E220.visualSharp", {"position": v(-597.2, 1701.8) * mm});
            skArc(sketch, "E220.filletArc", {"start": v(-622.6, 1701.8) * mm, "mid": v(-604.64, 1709.24) * mm, "end": v(-597.2, 1727.2) * mm});
            skPoint(sketch, "E221.visualSharp", {"position": v(-72.77, 1784.86) * mm});
            skArc(sketch, "E221.filletArc", {"start": v(-72.77, 1759.46) * mm, "mid": v(-80.21, 1777.42) * mm, "end": v(-98.17, 1784.86) * mm});
            skPoint(sketch, "E222.visualSharp", {"position": v(-72.77, 1701.8) * mm});
            skArc(sketch, "E222.filletArc", {"start": v(-72.77, 1727.2) * mm, "mid": v(-65.33, 1709.24) * mm, "end": v(-47.37, 1701.8) * mm});
            skArc(sketch, "E223.MirrorCS", {"start": v(72.77, 1727.2) * mm, "mid": v(65.33, 1709.24) * mm, "end": v(47.37, 1701.8) * mm});
            skArc(sketch, "E224.MirrorCS", {"start": v(622.6, 1701.8) * mm, "mid": v(604.64, 1709.24) * mm, "end": v(597.2, 1727.2) * mm});
            skArc(sketch, "E225.MirrorCS", {"start": v(72.77, 1759.46) * mm, "mid": v(80.21, 1777.42) * mm, "end": v(98.17, 1784.86) * mm});
            skPoint(sketch, "E226.MirrorP", {"position": v(334.99, 1784.86) * mm});
            skArc(sketch, "E227.MirrorCS", {"start": v(571.8, 1784.86) * mm, "mid": v(589.76, 1777.42) * mm, "end": v(597.2, 1759.46) * mm});
            skPoint(sketch, "E228.MirrorP", {"position": v(72.77, 1701.8) * mm});
            skPoint(sketch, "E229.MirrorP", {"position": v(72.77, 1784.86) * mm});
            skPoint(sketch, "E230.MirrorP", {"position": v(597.2, 1701.8) * mm});
            skPoint(sketch, "E231.MirrorP", {"position": v(597.2, 1784.86) * mm});
            skLineSegment(sketch, "E232.MirrorCS", {"start": v(597.2, 1701.8) * mm, "end": v(72.77, 1701.8) * mm, "construction": true});
            skLineSegment(sketch, "E233.MirrorCS", {"start": v(72.77, 1759.46) * mm, "end": v(72.77, 1727.2) * mm});
            skLineSegment(sketch, "E234.MirrorCS", {"start": v(571.8, 1784.86) * mm, "end": v(98.17, 1784.86) * mm});
            skLineSegment(sketch, "E235.MirrorCS", {"start": v(597.2, 1727.2) * mm, "end": v(597.2, 1759.46) * mm});
            skLineSegment(sketch, "E236", {"start": v(72.1, 1701.8) * mm, "end": v(596.98, 1701.8) * mm, "construction": true});
            skLineSegment(sketch, "E237", {"start": v(596.98, 1701.8) * mm, "end": v(691.95, 1701.8) * mm});
            skLineSegment(sketch, "E238", {"start": v(-334.99, 1784.86) * mm, "end": v(-334.99, 1034.03) * mm, "construction": true});
            skLineSegment(sketch, "E239", {"start": v(-702.74, 2286) * mm, "end": v(702.74, 2286) * mm});
            skLineSegment(sketch, "E240", {"start": v(-751.07, 2321.16) * mm, "end": v(-922.58, 2851.22) * mm});
            skLineSegment(sketch, "E241", {"start": v(751.07, 2321.16) * mm, "end": v(922.58, 2851.22) * mm});
            skPoint(sketch, "E242.visualSharp", {"position": v(-739.7, 2286) * mm});
            skArc(sketch, "E242.filletArc", {"start": v(-751.07, 2321.16) * mm, "mid": v(-732.62, 2295.72) * mm, "end": v(-702.74, 2286) * mm});
            skPoint(sketch, "E243.visualSharp", {"position": v(739.7, 2286) * mm});
            skArc(sketch, "E243.filletArc", {"start": v(702.74, 2286) * mm, "mid": v(732.62, 2295.72) * mm, "end": v(751.07, 2321.16) * mm});
            skPoint(sketch, "E244.visualSharp", {"position": v(-329.35, 254) * mm});
            skArc(sketch, "E244.filletArc", {"start": v(-329.35, 260.35) * mm, "mid": v(-327.5, 255.86) * mm, "end": v(-323, 254) * mm});
            skPoint(sketch, "E245.visualSharp", {"position": v(-423.33, 254) * mm});
            skArc(sketch, "E245.filletArc", {"start": v(-423.33, 260.35) * mm, "mid": v(-421.47, 255.86) * mm, "end": v(-416.98, 254) * mm});
            skPoint(sketch, "E246.visualSharp", {"position": v(-376.34, 254) * mm});
            skArc(sketch, "E246.filletArc", {"start": v(-376.34, 260.35) * mm, "mid": v(-374.48, 255.86) * mm, "end": v(-370, 254) * mm});
            skPoint(sketch, "E247.visualSharp", {"position": v(-385.23, -254) * mm});
            skArc(sketch, "E247.filletArc", {"start": v(-385.23, -260.35) * mm, "mid": v(-387.1, -255.86) * mm, "end": v(-391.58, -254) * mm});
            skPoint(sketch, "E248.visualSharp", {"position": v(-338.24, -254) * mm});
            skArc(sketch, "E248.filletArc", {"start": v(-338.24, -260.35) * mm, "mid": v(-340.1, -255.86) * mm, "end": v(-344.6, -254) * mm});
            skArc(sketch, "E249", {"start": v(-416.98, 254) * mm, "mid": v(-394.53, 263.3) * mm, "end": v(-385.23, 285.75) * mm});
            skPoint(sketch, "E249.centerSnap0", {"position": v(-385.23, 285.75) * mm});
            skArc(sketch, "E250", {"start": v(-370, 254) * mm, "mid": v(-347.54, 263.3) * mm, "end": v(-338.24, 285.75) * mm});
            skPoint(sketch, "E250.centerSnap0", {"position": v(-338.24, 285.75) * mm});
            skArc(sketch, "E251.MirrorCS", {"start": v(-391.58, -254) * mm, "mid": v(-414.03, -263.3) * mm, "end": v(-423.33, -285.75) * mm});
            skArc(sketch, "E252.MirrorCS", {"start": v(-344.6, -254) * mm, "mid": v(-367.04, -263.3) * mm, "end": v(-376.34, -285.75) * mm});
            skLineSegment(sketch, "E253", {"start": v(-385.23, 317.5) * mm, "end": v(-385.23, 330.2) * mm});
            skLineSegment(sketch, "E254", {"start": v(-385.23, 330.2) * mm, "end": v(-376.34, 330.2) * mm});
            skLineSegment(sketch, "E255", {"start": v(-376.34, 330.2) * mm, "end": v(-376.34, 317.5) * mm});
            skLineSegment(sketch, "E256", {"start": v(-338.24, 317.5) * mm, "end": v(-338.24, 330.2) * mm});
            skLineSegment(sketch, "E257", {"start": v(-338.24, 330.2) * mm, "end": v(-329.35, 330.2) * mm});
            skLineSegment(sketch, "E258", {"start": v(-329.35, 330.2) * mm, "end": v(-329.35, 317.5) * mm});
            skSolve(sketch);
        }
        {
            var Q0;
            Q0=makeQuery(id+"F0.imprint","IMPRINT",FACE,{"disambiguationData":[TD([[makeQuery(id+"F0.imprint","IMPRINT",EDGE,{"derivedFrom":sQuery(id+"F0.wireOp",EDGE,"E0.top")}),1.0]])]});
            var Q1;
            Q1=makeQuery(id+"F0.imprint","IMPRINT",FACE,{"disambiguationData":[TD([[makeQuery(id+"F0.imprint","IMPRINT",EDGE,{"derivedFrom":sQuery(id+"F0.wireOp",EDGE,"E21.bottom")}),1.0]])]});
            var Q2;
            Q2=makeQuery(id+"F0.imprint","IMPRINT",FACE,{"disambiguationData":[TD([[makeQuery(id+"F0.imprint","IMPRINT",EDGE,{"derivedFrom":sQuery(id+"F0.wireOp",EDGE,"E23.MirrorCS")}),1.0]])]});
            var Q3;
            Q3=makeQuery(id+"F0.imprint","IMPRINT",FACE,{"disambiguationData":[TD([[makeQuery(id+"F0.imprint","IMPRINT",EDGE,{"derivedFrom":sQuery(id+"F0.wireOp",EDGE,"f6738329-a918-480e-9177-daac320b32cd.bottom")}),-1.0]])]});
            var Q4;
            Q4=makeQuery(id+"F0.imprint","IMPRINT",FACE,{"disambiguationData":[TD([[makeQuery(id+"F0.imprint","IMPRINT",EDGE,{"derivedFrom":sQuery(id+"F0.wireOp",EDGE,"d69082ea-fb69-471d-a931-f7dcb4c410b10.MirrorCS")}),-1.0]])]});
            var Q5;
            Q5=makeQuery(id+"F0.imprint","IMPRINT",FACE,{"disambiguationData":[TD([[makeQuery(id+"F0.imprint","IMPRINT",EDGE,{"derivedFrom":sQuery(id+"F0.wireOp",EDGE,"6e7c8a08-07b1-41cb-9a36-e43f01201c65.bottom")}),1.0]])]});
            var Q6;
            Q6=makeQuery(id+"F0.imprint","IMPRINT",FACE,{"disambiguationData":[TD([[makeQuery(id+"F0.imprint","IMPRINT",EDGE,{"derivedFrom":sQuery(id+"F0.wireOp",EDGE,"ff26a79c-f42c-4c2e-a1a1-40e0c3ee671e")}),1.0]])]});
            var Q7;
            Q7=makeQuery(id+"F0.imprint","IMPRINT",FACE,{"disambiguationData":[TD([[makeQuery(id+"F0.imprint","IMPRINT",EDGE,{"derivedFrom":sQuery(id+"F0.wireOp",EDGE,"33e68a98-cf04-4dc6-9c8b-7573a09791d5.top")}),-1.0]])]});
            var Q8;
            Q8=makeQuery(id+"F0.imprint","IMPRINT",FACE,{"disambiguationData":[TD([[makeQuery(id+"F0.imprint","IMPRINT",EDGE,{"derivedFrom":sQuery(id+"F0.wireOp",EDGE,"857dc58a-d729-4c5a-bf12-05aab3a429b0.bottom")}),-1.0]])]});
            var Q9;
            Q9=makeQuery(id+"F0.imprint","IMPRINT",FACE,{"disambiguationData":[TD([[makeQuery(id+"F0.imprint","IMPRINT",EDGE,{"derivedFrom":sQuery(id+"F0.wireOp",EDGE,"705dcdab-93d6-4a35-a508-4c17f166d1d4.MirrorCS")}),-1.0]])]});
            var Q10;
            {var subQ11=sQuery(id+"F0.wireOp",EDGE,"4b4208f6-c2fb-4491-82b5-bbb72651a30f");Q10=makeQuery(id+"F0.imprint","IMPRINT",FACE,{"disambiguationData":[TD([[makeQuery(id+"F0.imprint","IMPRINT",EDGE,{"derivedFrom":subQ11}),1.0]])]});}
            var Q11;
            Q11=makeQuery(id+"F0.imprint","IMPRINT",FACE,{"disambiguationData":[TD([[makeQuery(id+"F0.imprint","IMPRINT",EDGE,{"derivedFrom":sQuery(id+"F0.wireOp",EDGE,"ZEEkujvX-f0nl-X2ht-5uEe-wjA7yF6qMzgc")}),1.0]])]});
            var Q12;
            {var subQ0=sQuery(id+"F0.wireOp",EDGE,"cHDWE3Ce-WObb-T2iv-pb7J-tTBgFW9YY9rB");Q12=makeQuery(id+"F0.imprint","IMPRINT",FACE,{"disambiguationData":[TD([[makeQuery(id+"F0.imprint","IMPRINT",EDGE,{"derivedFrom":subQ0}),-1.0]])]});}
            var Q13;
            Q13=makeQuery(id+"F0.imprint","IMPRINT",FACE,{"disambiguationData":[TD([[makeQuery(id+"F0.imprint","IMPRINT",EDGE,{"derivedFrom":sQuery(id+"F0.wireOp",EDGE,"80414a30-6be5-4261-b871-3fd237e30337.0")}),1.0]])]});
            var Q14;
            Q14=makeQuery(id+"F0.imprint","IMPRINT",FACE,{"disambiguationData":[TD([[makeQuery(id+"F0.imprint","IMPRINT",EDGE,{"derivedFrom":sQuery(id+"F0.wireOp",EDGE,"54f77c24-bd47-4d14-9fa3-259c3651231d.right")}),1.0]])]});
            var Q15;
            {var subQ4=sQuery(id+"F0.wireOp",EDGE,"E0.right");Q15=makeQuery(id+"F0.imprint","IMPRINT",FACE,{"disambiguationData":[TD([[makeQuery(id+"F0.imprint","IMPRINT",EDGE,{"derivedFrom":subQ4}),-1.0]])]});}
            var Q16;
            Q16=makeQuery(id+"F0.imprint","IMPRINT",FACE,{"disambiguationData":[TD([[makeQuery(id+"F0.imprint","IMPRINT",EDGE,{"derivedFrom":sQuery(id+"F0.wireOp",EDGE,"E143.bottom")}),-1.0]])]});
            var Q17;
            {var subQ17=sQuery(id+"F0.wireOp",EDGE,"E111.left");Q17=makeQuery(id+"F0.imprint","IMPRINT",FACE,{"disambiguationData":[TD([[makeQuery(id+"F0.imprint","IMPRINT",EDGE,{"derivedFrom":subQ17}),1.0]])]});}
            var Q18;
            Q18=makeQuery(id+"F0.imprint","IMPRINT",FACE,{"disambiguationData":[TD([[makeQuery(id+"F0.imprint","IMPRINT",EDGE,{"derivedFrom":sQuery(id+"F0.wireOp",EDGE,"E40")}),-1.0]])]});
            var Q19;
            Q19=makeQuery(id+"F0.imprint","IMPRINT",FACE,{"disambiguationData":[TD([[makeQuery(id+"F0.imprint","IMPRINT",EDGE,{"derivedFrom":sQuery(id+"F0.wireOp",EDGE,"E110.top")}),-1.0]])]});
            var Q20;
            {var subQ0=sQuery(id+"F0.wireOp",EDGE,"E115.MirrorCS");Q20=makeQuery(id+"F0.imprint","IMPRINT",FACE,{"disambiguationData":[TD([[makeQuery(id+"F0.imprint","IMPRINT",EDGE,{"derivedFrom":subQ0}),-1.0]])]});}
            var Q21;
            Q21=makeQuery(id+"F0.imprint","IMPRINT",FACE,{"disambiguationData":[TD([[makeQuery(id+"F0.imprint","IMPRINT",EDGE,{"derivedFrom":sQuery(id+"F0.wireOp",EDGE,"E130.bottom")}),1.0]])]});
            var Q22;
            Q22=makeQuery(id+"F0.imprint","IMPRINT",FACE,{"disambiguationData":[TD([[makeQuery(id+"F0.imprint","IMPRINT",EDGE,{"derivedFrom":sQuery(id+"F0.wireOp",EDGE,"E133.MirrorCS")}),-1.0]])]});
            var Q23;
            {var subQ0=sQuery(id+"F0.wireOp",EDGE,"E123.MirrorCS");Q23=makeQuery(id+"F0.imprint","IMPRINT",FACE,{"disambiguationData":[TD([[makeQuery(id+"F0.imprint","IMPRINT",EDGE,{"derivedFrom":subQ0}),-1.0]])]});}
            var Q24;
            Q24=makeQuery(id+"F0.imprint","IMPRINT",FACE,{"disambiguationData":[TD([[makeQuery(id+"F0.imprint","IMPRINT",EDGE,{"derivedFrom":sQuery(id+"F0.wireOp",EDGE,"E119.MirrorCS")}),1.0]])]});
            var Q25;
            Q25=makeQuery(id+"F0.imprint","IMPRINT",FACE,{"disambiguationData":[TD([[makeQuery(id+"F0.imprint","IMPRINT",EDGE,{"derivedFrom":sQuery(id+"F0.wireOp",EDGE,"E176.bottom")}),1.0]])]});
            var Q26;
            {var subQ0=sQuery(id+"F0.wireOp",EDGE,"E165.right");Q26=makeQuery(id+"F0.imprint","IMPRINT",FACE,{"disambiguationData":[TD([[makeQuery(id+"F0.imprint","IMPRINT",EDGE,{"derivedFrom":subQ0}),-1.0]])]});}
            var Q27;
            {var subQ0=sQuery(id+"F0.wireOp",EDGE,"E167.right");Q27=makeQuery(id+"F0.imprint","IMPRINT",FACE,{"disambiguationData":[TD([[makeQuery(id+"F0.imprint","IMPRINT",EDGE,{"derivedFrom":subQ0}),-1.0]])]});}
            var Q28;
            Q28=makeQuery(id+"F0.imprint","IMPRINT",FACE,{"disambiguationData":[TD([[makeQuery(id+"F0.imprint","IMPRINT",EDGE,{"derivedFrom":sQuery(id+"F0.wireOp",EDGE,"E202.bottom")}),-1.0]])]});
            var Q29;
            Q29=makeQuery(id+"F0.imprint","IMPRINT",FACE,{"disambiguationData":[TD([[makeQuery(id+"F0.imprint","IMPRINT",EDGE,{"derivedFrom":sQuery(id+"F0.wireOp",EDGE,"E203.bottom")}),-1.0]])]});
            var Q30;
            Q30=makeQuery(id+"F0.imprint","IMPRINT",FACE,{"disambiguationData":[TD([[makeQuery(id+"F0.imprint","IMPRINT",EDGE,{"derivedFrom":sQuery(id+"F0.wireOp",EDGE,"E204.MirrorCS")}),1.0]])]});
            var Q31;
            Q31=makeQuery(id+"F0.imprint","IMPRINT",FACE,{"disambiguationData":[TD([[makeQuery(id+"F0.imprint","IMPRINT",EDGE,{"derivedFrom":sQuery(id+"F0.wireOp",EDGE,"E187.MirrorCS")}),-1.0]])]});
            var Q32;
            Q32=makeQuery(id+"F0.imprint","IMPRINT",FACE,{"disambiguationData":[TD([[makeQuery(id+"F0.imprint","IMPRINT",EDGE,{"derivedFrom":sQuery(id+"F0.wireOp",EDGE,"E163.right")}),-1.0]])]});
            var Q33;
            Q33=makeQuery(id+"F0.imprint","IMPRINT",FACE,{"disambiguationData":[TD([[makeQuery(id+"F0.imprint","IMPRINT",EDGE,{"derivedFrom":sQuery(id+"F0.wireOp",EDGE,"E168.MirrorCS")}),-1.0]])]});
            var Q34;
            Q34=makeQuery(id+"F0.imprint","IMPRINT",FACE,{"disambiguationData":[TD([[makeQuery(id+"F0.imprint","IMPRINT",EDGE,{"derivedFrom":sQuery(id+"F0.wireOp",EDGE,"E167.bottom")}),1.0]])]});
            var Q35;
            Q35=makeQuery(id+"F0.imprint","IMPRINT",FACE,{"disambiguationData":[TD([[makeQuery(id+"F0.imprint","IMPRINT",EDGE,{"derivedFrom":sQuery(id+"F0.wireOp",EDGE,"E163.left")}),1.0]])]});
            var Q36;
            Q36=makeQuery(id+"F0.imprint","IMPRINT",FACE,{"disambiguationData":[TD([[makeQuery(id+"F0.imprint","IMPRINT",EDGE,{"derivedFrom":sQuery(id+"F0.wireOp",EDGE,"E165.bottom")}),1.0]])]});
            extrude(context, id + "F1", {"entities" : qUnion([Q0, Q1, Q2, Q3, Q4, Q5, Q6, Q7, Q8, Q9, Q10, Q11, Q12, Q13, Q14, Q15, Q16, Q17, Q18, Q19, Q20, Q21, Q22, Q23, Q24, Q25, Q26, Q27, Q28, Q29, Q30, Q31, Q32, Q33, Q34, Q35, Q36]), "depth" : 18.54 * mm});
        }
    });
